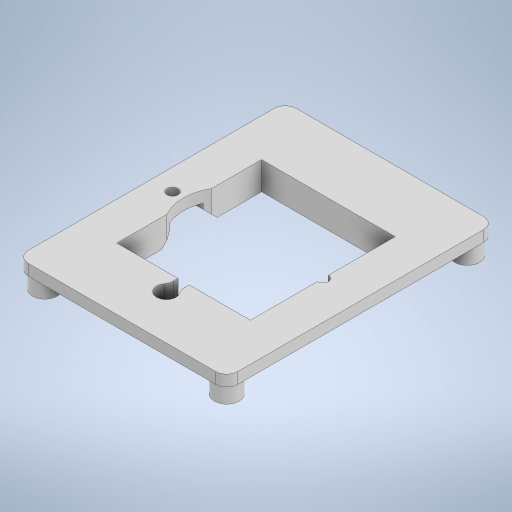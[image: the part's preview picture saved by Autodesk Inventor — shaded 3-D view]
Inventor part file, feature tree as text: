
AUTODESK INVENTOR PART (.ipt)
format: ipt  version: 2024.2 (Build 282272000, 272)  size: 375,296 bytes
history: native  units: mm
features: extrude x9, sketch x9, fillet x2, chamfer x1
ambient origin geometry x8: Origin, YZ Plane, XZ Plane, XY Plane, X Axis, Y Axis, Z Axis, Center Point
bodies: Solid1 (feature_tree)
feature tree (21):
  extrude  "Extrusion1"  Depth=38.5mm
  extrude  "Extrusion2"  Depth=26.0mm
  extrude  "Extrusion3"  Depth=3.0mm
  extrude  "Extrusion4"  Depth=4.0mm
  fillet  "Fillet1"  Radius=4.0mm
  extrude  "Extrusion6"  Depth=48.2mm
  extrude  "Extrusion7"  Depth=4.85mm
  chamfer  "Chamfer1"  Distance=2.0mm
  extrude  "Extrusion8"  Depth=2.35mm
  extrude  "Extrusion9"  Depth=2.0mm
  extrude  "Extrusion10"  Depth=2.0mm
  fillet  "Fillet2"  Radius=2.35mm
  sketch  "Sketch1"  dims[d0=28.0mm d1=38.5mm]
  sketch  "Sketch2"  dims[d2=24.0mm d3=26.0mm]
  sketch  "Sketch3"  dims[d6=3.0mm d7=0.0mm d8=4.0mm]
  sketch  "Sketch4"  dims[d9=4.0mm d10=4.0mm d11=4.0mm]
  sketch  "Sketch5"  dims[d12=3.0mm d13=0.0mm d14=48.2mm]
  sketch  "Sketch6"  dims[d15=37.7mm d16=4.85mm]
  sketch  "Sketch7"  dims[d17=4.85mm d18=2.0mm d19=0.0mm]
  sketch  "Sketch8"  dims[d20=4.5mm d21=2.35mm]
  sketch  "Sketch9"  dims[d22=2.35mm d23=4.5mm d24=2.35mm d25=2.35mm d26=4.5mm d27=2.35mm d28=4.5mm d29=2.35mm d30=2.35mm d31=2.35mm d32=3.0mm d33=0.0mm d34=2.0mm d43=2.0mm d44=6.25mm d45=2.0mm d46=2.0mm d47=13.0mm d50=13.0mm d51=0.0mm d52=0.0mm d53=6.0mm d54=21.1mm d55=10.0mm d56=0.0mm d57=2.0mm d58=2.0mm d59=45.0deg d63=8.0mm d64=20.1mm d65=8.0mm d66=10.0mm d67=0.0mm d68=3.5mm d69=3.125mm d70=18.85mm d71=0.0mm d72=0.0mm d73=27.0mm d75=3.0mm d76=2.0mm d77=1.0mm d78=0.0mm d79=0.0mm d80=2.0mm]
